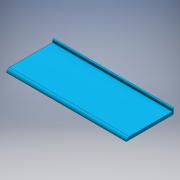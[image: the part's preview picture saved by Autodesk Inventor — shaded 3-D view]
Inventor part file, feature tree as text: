
AUTODESK INVENTOR PART (.ipt)
format: ipt  version: 2016 (Build 200138000, 138)  size: 135,168 bytes
history: native  units: mm
features: extrude x2, sketch x2, fillet x1
ambient origin geometry x8: Origin, YZ Plane, XZ Plane, XY Plane, X Axis, Y Axis, Z Axis, Center Point
bodies: Solid1 (feature_tree)
feature tree (5):
  extrude  "Extrusion1"  Depth=50.0mm TaperAngle=0.0deg
  fillet  "Fillet1"  Radius=50.0mm
  extrude  "Extrusion2"  Depth=20.0mm
  sketch  "Sketch1"  dims[d1=790.0mm d2=50.0mm d3=0.0mm d4=50.0mm]
  sketch  "Sketch2"  dims[d5=100.0mm d6=20.0mm d7=20.0mm d8=50.0mm d9=0.0mm]
